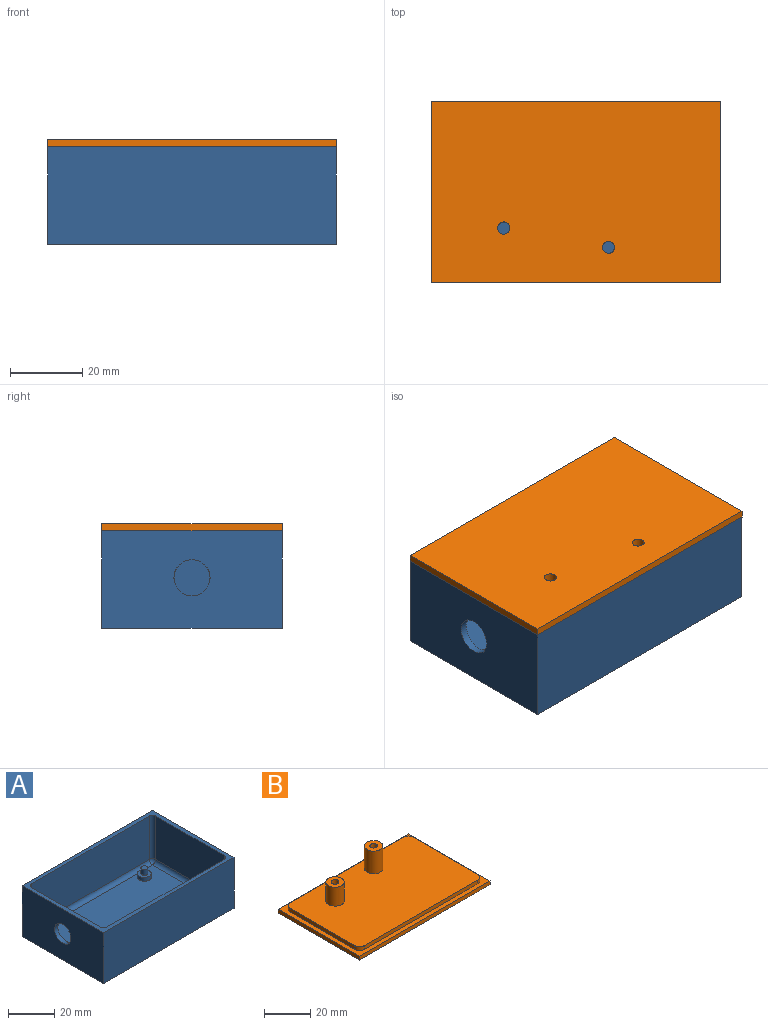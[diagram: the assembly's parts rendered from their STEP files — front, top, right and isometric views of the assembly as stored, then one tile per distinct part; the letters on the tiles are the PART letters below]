
ASSEMBLY  parts=2 mates=1
PART A: 40 faces, bbox 80x50x27 mm
  f0: plane 80x50mm, normal (0,0,1), area 507.4mm2, adj f1,f2,f3,f4,f6,f7,f8,f9
  f1: plane 80x27mm, normal (0,-1,0), area 2160mm2, adj f0,f2,f4,f5
  f2: plane 50x27mm, normal (1,0,0), area 1350mm2, adj f0,f1,f3,f5
  f3: plane 80x27mm, normal (0,1,0), area 2160mm2, adj f0,f2,f4,f5
  f4: plane 50x27mm, normal (-1,0,0), area 1271.5mm2, adj f0,f1,f3,f5,f19
  f5: plane 80x50mm, normal (0,0,-1), area 4000mm2, adj f1,f2,f3,f4
  f6: plane 72x23mm, normal (0,1,0), area 1656mm2, adj f0,f22,f28,f31
  f7: plane 42x23mm, normal (-1,0,0), area 966mm2, adj f0,f25,f29,f31
  f8: plane 72x23mm, normal (0,-1,0), area 1656mm2, adj f0,f20,f24,f25
  f9: plane 42x23mm, normal (1,0,0), area 887.5mm2, adj f0,f19,f20,f22,f23
  f10: plane 72x42mm, normal (0,0,1), area 2910.9mm2, adj f11,f13,f15,f17,f23,f24,f28,f29
  f11: cylinder r=3mm len=6mm, axis (0,0,-1), area 37.7mm2, adj f10,f12
  f12: plane 6x6mm, normal (0,0,1), area 21.2mm2, adj f11,f34
  f13: cylinder r=3mm len=6mm, axis (0,0,-1), area 37.7mm2, adj f10,f14
  f14: plane 6x6mm, normal (0,0,1), area 21.2mm2, adj f13,f36
  f15: cylinder r=3mm len=6mm, axis (0,0,-1), area 37.7mm2, adj f10,f16
  f16: plane 6x6mm, normal (0,0,1), area 21.2mm2, adj f15,f32
  f17: cylinder r=3mm len=6mm, axis (0,0,-1), area 37.7mm2, adj f10,f18
  f18: plane 6x6mm, normal (0,0,1), area 21.2mm2, adj f17,f38
  f19: cylinder r=5mm len=10mm, axis (-1,0,0), area 62.8mm2, adj f4,f9
  f20: cylinder r=2mm len=23mm, axis (0,0,1), area 72.3mm2, adj f0,f8,f9,f21
  f21: sphere r=2mm, area 6.3mm2, adj f20,f23,f24
  f22: cylinder r=2mm len=23mm, axis (0,0,-1), area 72.3mm2, adj f0,f6,f9,f26
  f23: cylinder r=2mm len=42mm, axis (0,-1,0), area 131.9mm2, adj f9,f10,f21,f26
  f24: cylinder r=2mm len=72mm, axis (-1,0,0), area 226.2mm2, adj f8,f10,f21,f27
  f25: cylinder r=2mm len=23mm, axis (0,0,-1), area 72.3mm2, adj f0,f7,f8,f27
  f26: sphere r=2mm, area 6.3mm2, adj f22,f23,f28
  f27: sphere r=2mm, area 6.3mm2, adj f24,f25,f29
  f28: cylinder r=2mm len=72mm, axis (1,0,0), area 226.2mm2, adj f6,f10,f26,f30
  f29: cylinder r=2mm len=42mm, axis (0,1,0), area 131.9mm2, adj f7,f10,f27,f30
  f30: sphere r=2mm, area 6.3mm2, adj f28,f29,f31
  f31: cylinder r=2mm len=23mm, axis (0,0,1), area 72.3mm2, adj f0,f6,f7,f30
  f32: cylinder r=1.5mm len=3mm, axis (0,0,-1), area 28.3mm2, adj f16,f33
  f33: plane 3x3mm, normal (0,0,1), area 7.1mm2, adj f32
  f34: cylinder r=1.5mm len=3mm, axis (0,0,-1), area 28.3mm2, adj f12,f35
  f35: plane 3x3mm, normal (0,0,1), area 7.1mm2, adj f34
  f36: cylinder r=1.5mm len=3mm, axis (0,0,-1), area 28.3mm2, adj f14,f37
  f37: plane 3x3mm, normal (0,0,1), area 7.1mm2, adj f36
  f38: cylinder r=1.5mm len=3mm, axis (0,0,-1), area 28.3mm2, adj f18,f39
  f39: plane 3x3mm, normal (0,0,1), area 7.1mm2, adj f38
PART B: 21 faces, bbox 80x50x16 mm
  f0: plane 80x50mm, normal (0,0,1), area 560.4mm2, adj f1,f2,f3,f4,f6,f7,f8,f9
  f1: plane 80x2mm, normal (0,-1,0), area 160mm2, adj f0,f2,f4,f5
  f2: plane 50x2mm, normal (1,0,0), area 100mm2, adj f0,f1,f3,f5
  f3: plane 80x2mm, normal (0,1,0), area 160mm2, adj f0,f2,f4,f5
  f4: plane 50x2mm, normal (-1,0,0), area 100mm2, adj f0,f1,f3,f5
  f5: plane 80x50mm, normal (0,0,-1), area 3982.4mm2, adj f1,f2,f3,f4,f15,f16
  f6: plane 69.6x2mm, normal (0,-1,0), area 139.2mm2, adj f0,f10,f11,f14
  f7: plane 39.6x2mm, normal (1,0,0), area 79.2mm2, adj f0,f10,f11,f12
  f8: plane 69.6x2mm, normal (0,1,0), area 139.2mm2, adj f0,f10,f12,f13
  f9: plane 39.6x2mm, normal (-1,0,0), area 79.2mm2, adj f0,f10,f13,f14
  f10: plane 75.6x45.6mm, normal (0,0,1), area 3339.1mm2, adj f6,f7,f8,f9,f11,f12,f13,f14
  f11: cylinder r=3mm len=3mm, axis (0,0,1), area 9.4mm2, adj f0,f6,f7,f10
  f12: cylinder r=3mm len=3mm, axis (0,0,-1), area 9.4mm2, adj f0,f7,f8,f10
  f13: cylinder r=3mm len=3mm, axis (0,0,1), area 9.4mm2, adj f0,f8,f9,f10
  f14: cylinder r=3mm len=3mm, axis (0,0,-1), area 9.4mm2, adj f0,f6,f9,f10
  f15: cylinder r=1.65mm len=16mm, axis (0,0,-1), area 165.9mm2, adj f5,f18
  f16: cylinder r=1.7mm len=14mm, axis (0,0,-1), area 149.5mm2, adj f5,f20
  f17: cylinder r=4mm len=12mm, axis (0,0,-1), area 301.6mm2, adj f10,f18
  f18: plane 8x8mm, normal (0,0,1), area 41.7mm2, adj f15,f17
  f19: cylinder r=4mm len=10mm, axis (0,0,-1), area 251.3mm2, adj f10,f20
  f20: plane 8x8mm, normal (0,0,1), area 41.2mm2, adj f16,f19
PLACE A t=(-62.55,-14.39,-34.74)mm
PLACE B rot(axis=(1,0,0),180deg) t=(-62.55,-14.39,-5.74)mm
MATE fastened B.f0 <-> A.f0  axis (0,0,-1) through (-102.55,-39.39,-7.74)mm
